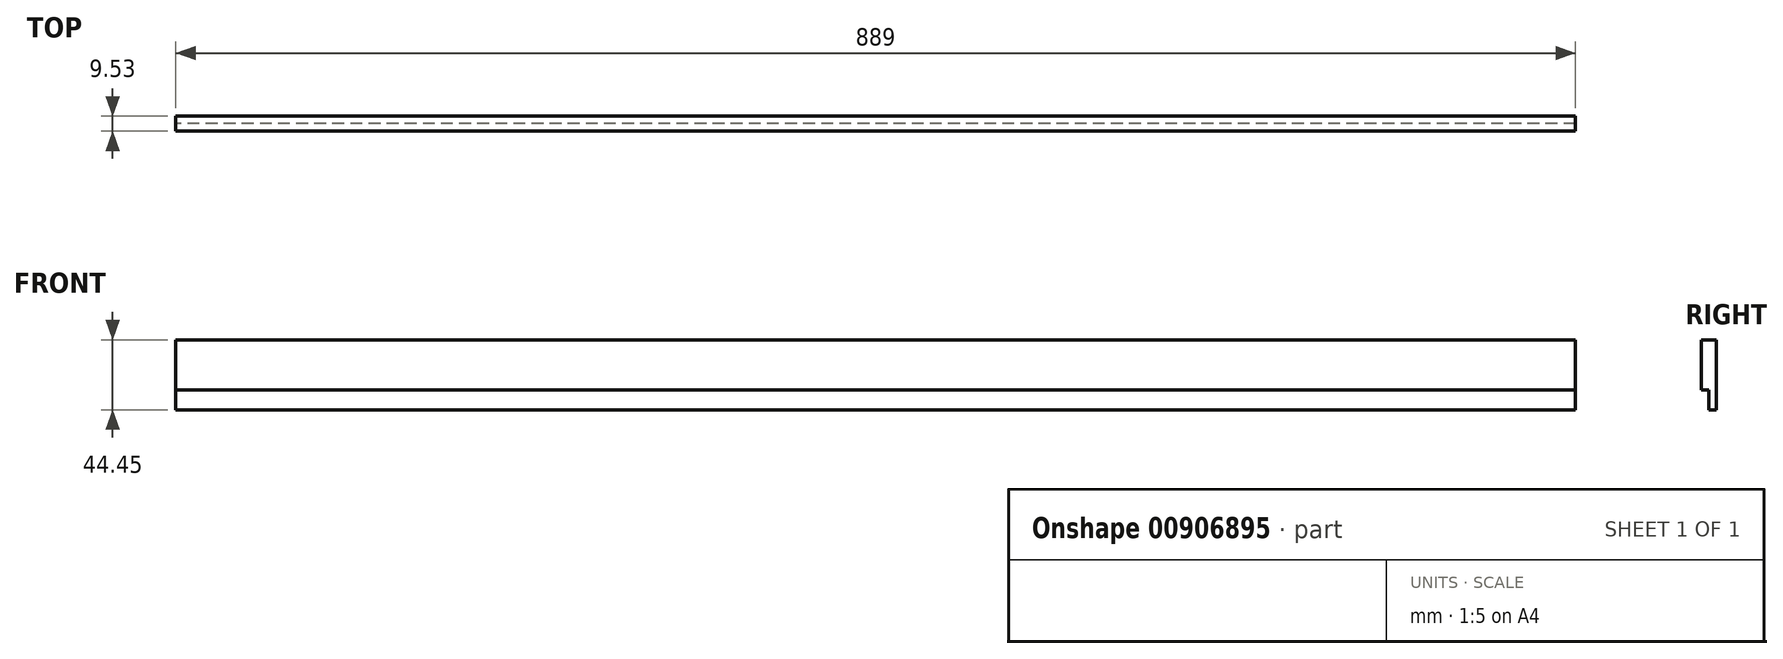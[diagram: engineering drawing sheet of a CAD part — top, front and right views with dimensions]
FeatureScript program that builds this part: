
annotation { "Feature Type Name" : "Feature", "Feature Type Description" : "" }
export const myFeature = defineFeature(function(context is Context, id is Id, definition is map)
    precondition{}
    {
        {
            var Q0;
            Q0=qCreatedBy(makeId("Right.planeOp"),FACE);
            var sketch = newSketch(context, id + "F0", { "sketchPlane" : qUnion([Q0])});
            skLineSegment(sketch, "E0", {"start": v(9.53, 0) * mm, "end": v(9.53, 44.45) * mm});
            skLineSegment(sketch, "E1", {"start": v(9.53, 44.45) * mm, "end": v(0, 44.45) * mm});
            skLineSegment(sketch, "E2", {"start": v(0, 12.7) * mm, "end": v(4.76, 12.7) * mm});
            skLineSegment(sketch, "E3", {"start": v(4.76, 12.7) * mm, "end": v(4.76, 0) * mm});
            skLineSegment(sketch, "E4", {"start": v(0, 44.45) * mm, "end": v(0, 12.7) * mm});
            skLineSegment(sketch, "E5", {"start": v(4.76, 0) * mm, "end": v(9.53, 0) * mm});
            skSolve(sketch);
        }
        {
            var Q0;
            Q0 = qSketchRegion(id + "F0", true);
            extrude(context, id + "F1", {"entities" : qUnion([Q0]), "endBound" : BoundingType.SYMMETRIC, "depth" : 889 * mm, "offsetDistance" : 25.4 * mm});
        }
    });
